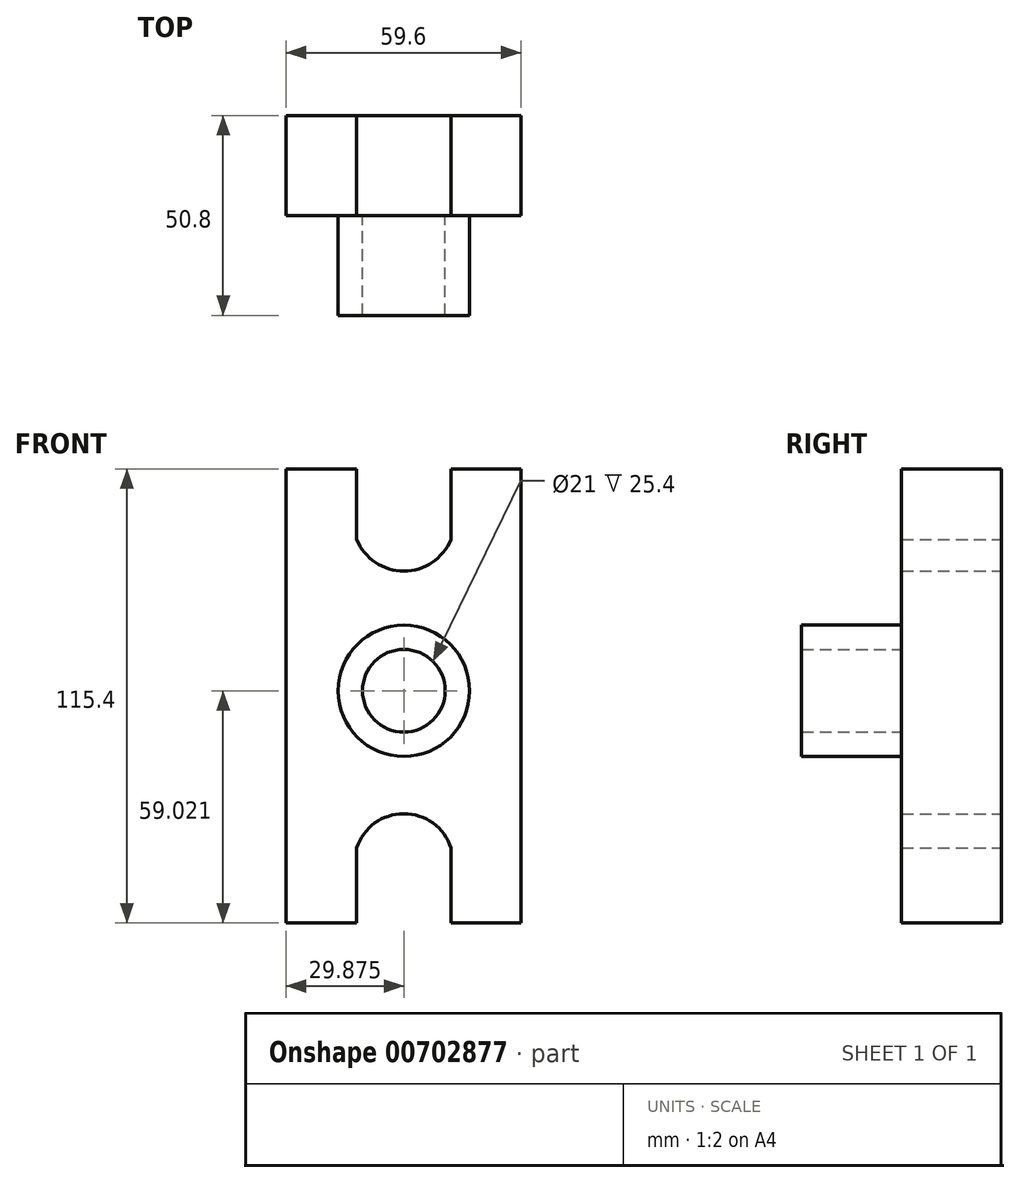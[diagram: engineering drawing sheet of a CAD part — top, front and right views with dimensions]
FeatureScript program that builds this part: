
annotation { "Feature Type Name" : "Feature", "Feature Type Description" : "" }
export const myFeature = defineFeature(function(context is Context, id is Id, definition is map)
    precondition{}
    {
        {
            var Q0;
            Q0=qCreatedBy(makeId("Front.planeOp"),FACE);
            var sketch = newSketch(context, id + "F0", { "sketchPlane" : qUnion([Q0])});
            skLineSegment(sketch, "E0.bottom", {"start": v(-41.84, 61.37) * mm, "end": v(-23.93, 61.37) * mm});
            skLineSegment(sketch, "E0.top", {"start": v(-41.84, -54.03) * mm, "end": v(-23.93, -54.03) * mm});
            skLineSegment(sketch, "E0.left", {"start": v(-41.84, 61.37) * mm, "end": v(-41.84, -54.03) * mm});
            skLineSegment(sketch, "E0.right", {"start": v(17.76, 61.37) * mm, "end": v(17.76, -54.03) * mm});
            skPoint(sketch, "E1", {"position": v(-23.93, 61.37) * mm});
            skPoint(sketch, "E2", {"position": v(0, 61.37) * mm});
            skLineSegment(sketch, "E3.trimOffspring", {"start": v(0, 61.37) * mm, "end": v(17.76, 61.37) * mm});
            skLineSegment(sketch, "E4", {"start": v(-23.93, 61.37) * mm, "end": v(-23.93, 43.45) * mm});
            skLineSegment(sketch, "E5", {"start": v(0, 61.37) * mm, "end": v(0, 43.45) * mm});
            skArc(sketch, "E6", {"start": v(-23.93, 43.45) * mm, "mid": v(-11.96, 35.4) * mm, "end": v(0, 43.45) * mm});
            skPoint(sketch, "E7", {"position": v(-23.93, -54.03) * mm});
            skPoint(sketch, "E8", {"position": v(0, -54.03) * mm});
            skLineSegment(sketch, "E9.trimOffspring", {"start": v(0, -54.03) * mm, "end": v(17.76, -54.03) * mm});
            skLineSegment(sketch, "E10", {"start": v(-23.93, -54.03) * mm, "end": v(-23.93, -34.94) * mm});
            skLineSegment(sketch, "E11", {"start": v(0, -54.03) * mm, "end": v(0, -34.94) * mm});
            skArc(sketch, "E12", {"start": v(0, -34.94) * mm, "mid": v(-11.96, -26.24) * mm, "end": v(-23.93, -34.94) * mm});
            skSolve(sketch);
        }
        {
            var Q0;
            Q0 = qSketchRegion(id + "F0", true);
            extrude(context, id + "F1", {"entities" : qUnion([Q0]), "depth" : 25.4 * mm, "offsetDistance" : 25.4 * mm});
        }
        {
            var Q0;
            Q0=makeQuery(id+"F1.opExtrude","CAP_FACE",FACE,{"disambiguationData":[OSD([sQuery(id+"F0.wireOp",EDGE,"E0.bottom"),sQuery(id+"F0.wireOp",EDGE,"E0.top"),sQuery(id+"F0.wireOp",EDGE,"E0.left"),sQuery(id+"F0.wireOp",EDGE,"E0.right"),sQuery(id+"F0.wireOp",EDGE,"E3.trimOffspring"),sQuery(id+"F0.wireOp",EDGE,"E4"),sQuery(id+"F0.wireOp",EDGE,"E5"),sQuery(id+"F0.wireOp",EDGE,"E6"),sQuery(id+"F0.wireOp",EDGE,"E9.trimOffspring"),sQuery(id+"F0.wireOp",EDGE,"E10"),sQuery(id+"F0.wireOp",EDGE,"E11"),sQuery(id+"F0.wireOp",EDGE,"E12")])],"isStart":false});
            var sketch = newSketch(context, id + "F2", { "sketchPlane" : qUnion([Q0])});
            skCircle(sketch, "E13", {"center": v(-11.96, 5) * mm, "radius": 16.68 * mm});
            skPoint(sketch, "E13.centerSnap0", {"position": v(-11.96, -26.24) * mm});
            skCircle(sketch, "E14", {"center": v(-11.96, 5) * mm, "radius": 10.5 * mm});
            skSolve(sketch);
        }
        {
            var Q0;
            Q0 = qSketchRegion(id + "F2", true);
            extrude(context, id + "F3", {"entities" : qUnion([Q0]), "operationType" : NewBodyOperationType.ADD, "depth" : 25.4 * mm, "offsetDistance" : 25.4 * mm});
        }
    });
